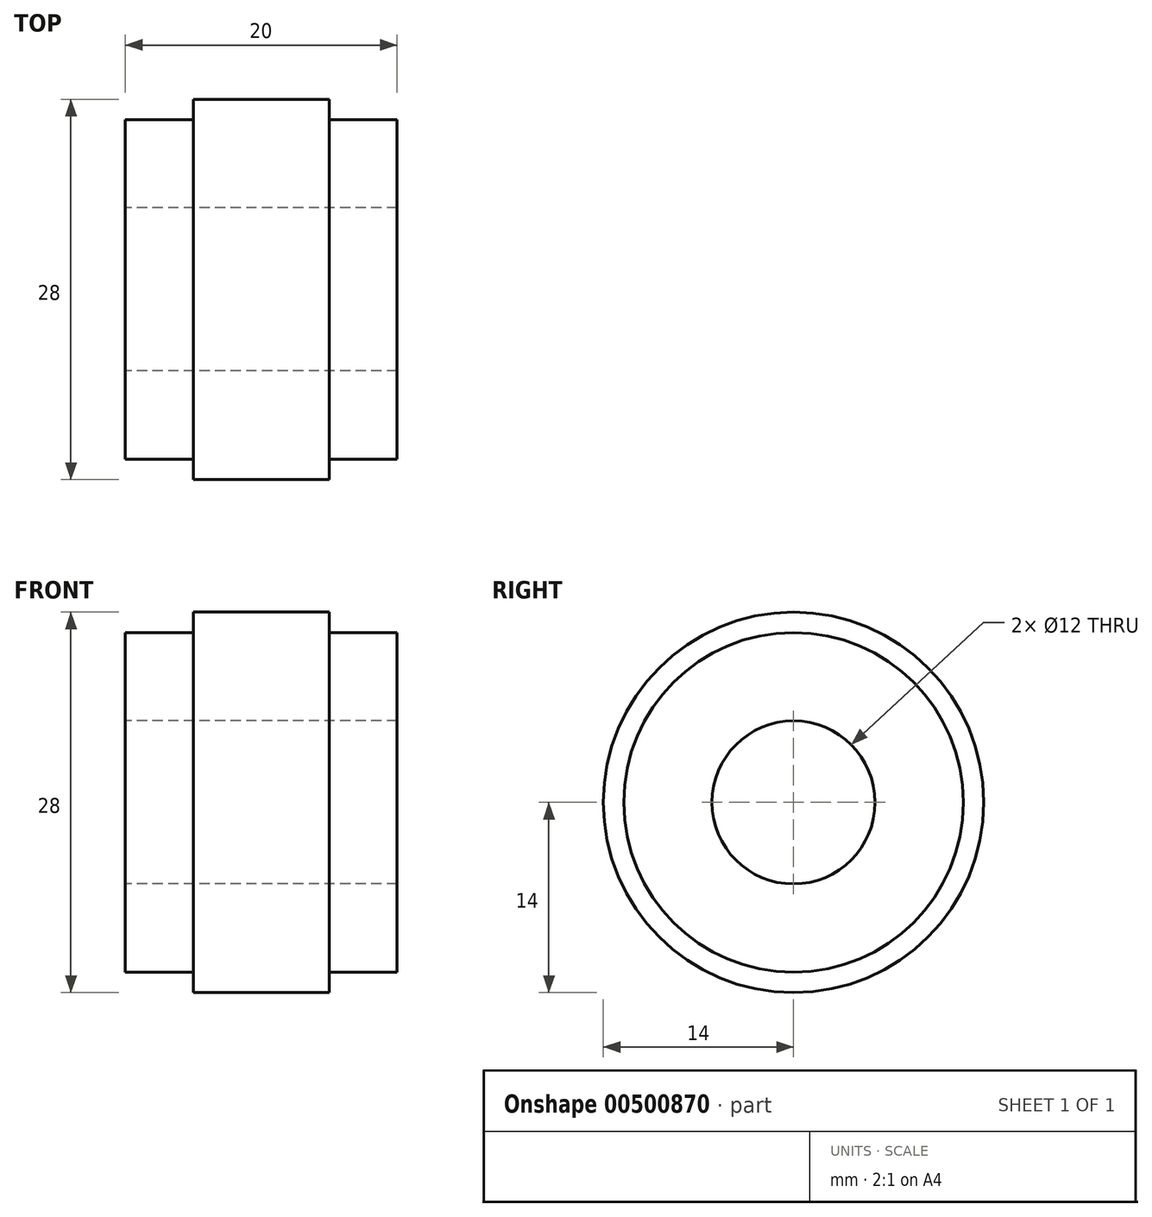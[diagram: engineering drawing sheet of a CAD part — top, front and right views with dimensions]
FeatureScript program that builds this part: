
annotation { "Feature Type Name" : "Feature", "Feature Type Description" : "" }
export const myFeature = defineFeature(function(context is Context, id is Id, definition is map)
    precondition{}
    {
        {
            var Q0;
            Q0=qCreatedBy(makeId("Front.planeOp"),FACE);
            var sketch = newSketch(context, id + "F0", { "sketchPlane" : qUnion([Q0])});
            skLineSegment(sketch, "E0", {"start": v(0, 0) * mm, "end": v(20, 0) * mm});
            skLineSegment(sketch, "E1", {"start": v(20, 0) * mm, "end": v(20, 12.5) * mm});
            skLineSegment(sketch, "E2", {"start": v(20, 12.5) * mm, "end": v(15, 12.5) * mm});
            skLineSegment(sketch, "E3", {"start": v(15, 12.5) * mm, "end": v(15, 14) * mm});
            skLineSegment(sketch, "E4", {"start": v(15, 14) * mm, "end": v(5, 14) * mm});
            skLineSegment(sketch, "E5", {"start": v(5, 14) * mm, "end": v(5, 12.5) * mm});
            skLineSegment(sketch, "E6", {"start": v(5, 12.5) * mm, "end": v(0, 12.5) * mm});
            skLineSegment(sketch, "E7", {"start": v(0, 12.5) * mm, "end": v(0, 0) * mm});
            skLineSegment(sketch, "E8", {"start": v(0, 6) * mm, "end": v(20, 6) * mm});
            skSolve(sketch);
        }
        {
            var Q0;
            {var subQ0=sQuery(id+"F0.wireOp",EDGE,"E2");Q0=makeQuery(id+"F0.imprint","IMPRINT",FACE,{"disambiguationData":[TD([[makeQuery(id+"F0.imprint","IMPRINT",EDGE,{"derivedFrom":subQ0}),1.0]])]});}
            var Q1;
            Q1=sQuery(id+"F0.wireOp",EDGE,"E0");
            revolve(context, id + "F1", {"entities" : qUnion([Q0]), "axis" : qUnion([Q1]), "revolveType" : RevolveType.FULL});
        }
    });
